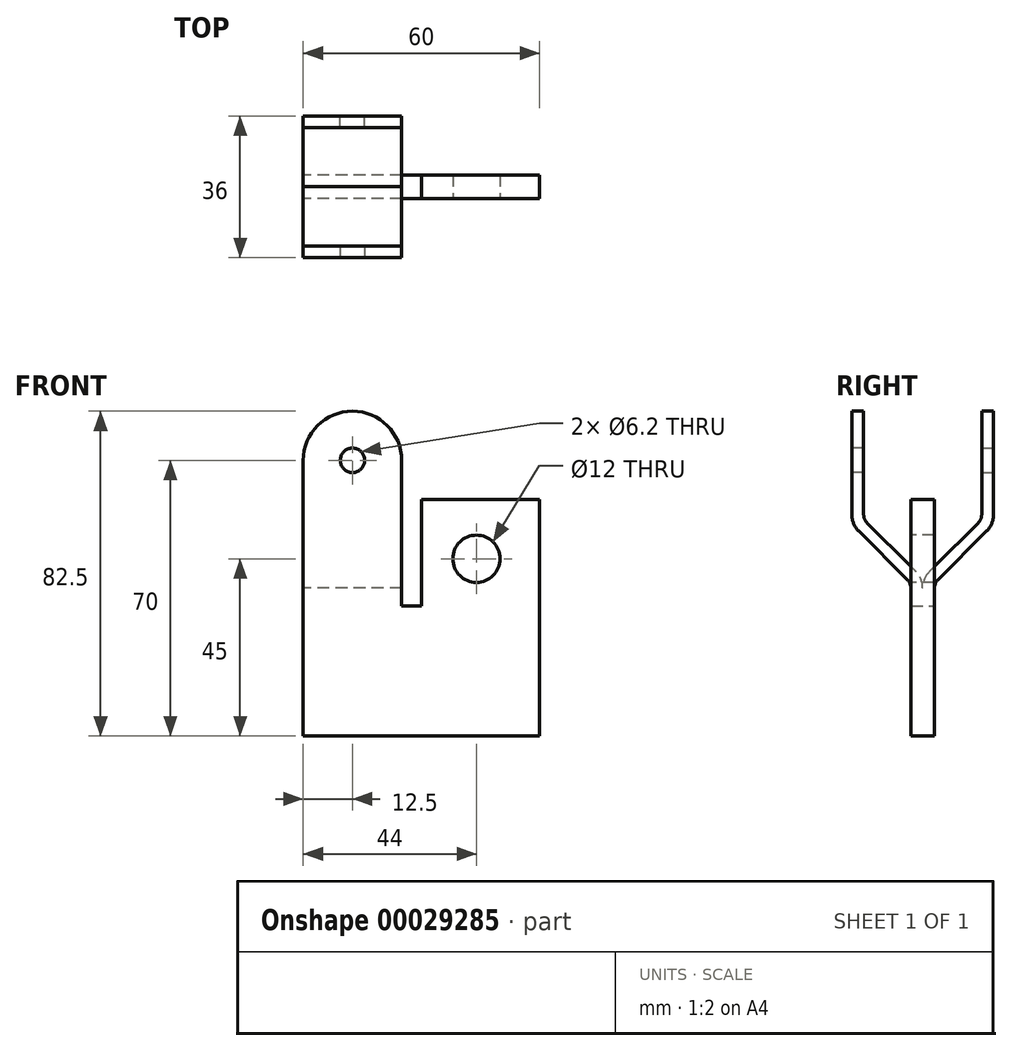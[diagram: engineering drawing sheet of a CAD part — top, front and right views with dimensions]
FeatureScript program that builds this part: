
annotation { "Feature Type Name" : "Feature", "Feature Type Description" : "" }
export const myFeature = defineFeature(function(context is Context, id is Id, definition is map)
    precondition{}
    {
        {
            var Q0;
            Q0=qCreatedBy(makeId("Front.planeOp"),FACE);
            var sketch = newSketch(context, id + "F0", { "sketchPlane" : qUnion([Q0])});
            skLineSegment(sketch, "E0", {"start": v(0, 0) * mm, "end": v(60, 0) * mm});
            skLineSegment(sketch, "E1", {"start": v(60, 0) * mm, "end": v(60, 60) * mm});
            skLineSegment(sketch, "E2", {"start": v(60, 60) * mm, "end": v(30, 60) * mm});
            skLineSegment(sketch, "E3", {"start": v(30, 60) * mm, "end": v(30, 33) * mm});
            skLineSegment(sketch, "E4", {"start": v(30, 33) * mm, "end": v(25, 33) * mm});
            skLineSegment(sketch, "E5", {"start": v(25, 33) * mm, "end": v(25, 35) * mm});
            skLineSegment(sketch, "E6", {"start": v(25, 35) * mm, "end": v(0, 35) * mm});
            skLineSegment(sketch, "E7", {"start": v(0, 35) * mm, "end": v(0, 0) * mm});
            skSolve(sketch);
        }
        {
            var Q0;
            Q0 = qSketchRegion(id + "F0", true);
            extrude(context, id + "F1", {"entities" : qUnion([Q0]), "depth" : 3 * mm});
        }
        {
            var Q0;
            Q0=makeQuery(id+"F1.opExtrude","SWEPT_FACE",FACE,{"disambiguationData":[OSD([sQuery(id+"F0.wireOp",EDGE,"E7")])]});
            var sketch = newSketch(context, id + "F2", { "sketchPlane" : qUnion([Q0])});
            skLineSegment(sketch, "E8", {"start": v(0, 35) * mm, "end": v(0, 40) * mm});
            skLineSegment(sketch, "E9", {"start": v(0, 40) * mm, "end": v(15, 55) * mm});
            skLineSegment(sketch, "E10", {"start": v(15, 55) * mm, "end": v(15, 82.5) * mm});
            skLineSegment(sketch, "E11", {"start": v(15, 82.5) * mm, "end": v(18, 82.5) * mm});
            skLineSegment(sketch, "E12", {"start": v(18, 82.5) * mm, "end": v(18, 53.76) * mm});
            skLineSegment(sketch, "E13", {"start": v(18, 53.76) * mm, "end": v(3, 38.76) * mm});
            skLineSegment(sketch, "E14", {"start": v(3, 38.76) * mm, "end": v(3, 35) * mm});
            skLineSegment(sketch, "E15", {"start": v(3, 35) * mm, "end": v(0, 35) * mm});
            skSolve(sketch);
        }
        {
            var Q0;
            Q0 = qSketchRegion(id + "F2", true);
            var Q1;
            Q1=makeQuery(id+"F1.opExtrude","SWEPT_FACE",FACE,{"disambiguationData":[OSD([sQuery(id+"F0.wireOp",EDGE,"E5")])]});
            extrude(context, id + "F3", {"entities" : qUnion([Q0]), "endBound" : BoundingType.UP_TO_SURFACE, "oppositeDirection" : true, "endBoundEntityFace" : qUnion([Q1]), "depth" : 25 * mm});
        }
        {
            var Q0;
            Q0=makeQuery(id+"F3.opExtrude","SWEPT_BODY",BODY,{"disambiguationData":[OSD([sQuery(id+"F2.wireOp",EDGE,"E8"),sQuery(id+"F2.wireOp",EDGE,"E9"),sQuery(id+"F2.wireOp",EDGE,"E10"),sQuery(id+"F2.wireOp",EDGE,"E11"),sQuery(id+"F2.wireOp",EDGE,"E12"),sQuery(id+"F2.wireOp",EDGE,"E13"),sQuery(id+"F2.wireOp",EDGE,"E14"),sQuery(id+"F2.wireOp",EDGE,"E15")])]});
            var Q1;
            Q1=makeQuery(id+"F1.opExtrude","SWEPT_BODY",BODY,{"disambiguationData":[OSD([sQuery(id+"F0.wireOp",EDGE,"E0"),sQuery(id+"F0.wireOp",EDGE,"E1"),sQuery(id+"F0.wireOp",EDGE,"E2"),sQuery(id+"F0.wireOp",EDGE,"E3"),sQuery(id+"F0.wireOp",EDGE,"E4"),sQuery(id+"F0.wireOp",EDGE,"E5"),sQuery(id+"F0.wireOp",EDGE,"E6"),sQuery(id+"F0.wireOp",EDGE,"E7")])]});
            booleanBodies(context, id + "F4", {"operationType" : BooleanOperationType.UNION, "tools" : qUnion([Q0, Q1])});
        }
        {
            var Q0;
            Q0=makeQuery(id+"F3.opExtrude","SWEPT_EDGE",EDGE,{"disambiguationData":[OSD([sQuery(id+"F2.wireOp",EDGE,"E13"),sQuery(id+"F2.wireOp",EDGE,"E14")])]});
            var Q1;
            Q1=makeQuery(id+"F3.opExtrude","SWEPT_EDGE",EDGE,{"disambiguationData":[OSD([sQuery(id+"F2.wireOp",EDGE,"E9"),sQuery(id+"F2.wireOp",EDGE,"E10")])]});
            fillet(context, id + "F5", {"entities" : qUnion([Q0, Q1]), "radius" : 3 * mm, "tangentPropagation" : true, "allowEdgeOverflow" : false});
        }
        {
            var Q0;
            Q0=makeQuery(id+"F3.opExtrude","SWEPT_EDGE",EDGE,{"disambiguationData":[OSD([sQuery(id+"F2.wireOp",EDGE,"E8"),sQuery(id+"F2.wireOp",EDGE,"E9")])]});
            var Q1;
            Q1=makeQuery(id+"F3.opExtrude","SWEPT_EDGE",EDGE,{"disambiguationData":[OSD([sQuery(id+"F2.wireOp",EDGE,"E12"),sQuery(id+"F2.wireOp",EDGE,"E13")])]});
            fillet(context, id + "F6", {"entities" : qUnion([Q0, Q1]), "radius" : 6 * mm, "tangentPropagation" : true, "allowEdgeOverflow" : false});
        }
        {
            var Q0;
            Q0=makeQuery(id+"F3.opExtrude","SWEPT_FACE",FACE,{"disambiguationData":[OSD([sQuery(id+"F2.wireOp",EDGE,"E12")])]});
            var sketch = newSketch(context, id + "F7", { "sketchPlane" : qUnion([Q0])});
            skCircle(sketch, "E16", {"center": v(12.5, 70) * mm, "radius": 3.1 * mm});
            skSolve(sketch);
        }
        {
            var Q0;
            Q0 = qSketchRegion(id + "F7", true);
            extrude(context, id + "F8", {"entities" : qUnion([Q0]), "operationType" : NewBodyOperationType.REMOVE, "endBound" : BoundingType.UP_TO_NEXT, "oppositeDirection" : true, "depth" : 25 * mm});
        }
        {
            var Q0;
            Q0=makeQuery(id+"F3.opExtrude","CAP_EDGE",EDGE,{"disambiguationData":[OSD([sQuery(id+"F2.wireOp",EDGE,"E11")])],"isStart":true});
            var Q1;
            Q1=makeQuery(id+"F3.opExtrude","CAP_EDGE",EDGE,{"disambiguationData":[OSD([sQuery(id+"F2.wireOp",EDGE,"E11")])],"isStart":false});
            fillet(context, id + "F9", {"entities" : qUnion([Q0, Q1]), "radius" : 12.5 * mm, "tangentPropagation" : true, "allowEdgeOverflow" : false});
        }
        {
            var Q0;
            Q0=makeQuery(id+"F3.opExtrude","SWEPT_BODY",BODY,{"disambiguationData":[OSD([sQuery(id+"F2.wireOp",EDGE,"E8"),sQuery(id+"F2.wireOp",EDGE,"E9"),sQuery(id+"F2.wireOp",EDGE,"E10"),sQuery(id+"F2.wireOp",EDGE,"E11"),sQuery(id+"F2.wireOp",EDGE,"E12"),sQuery(id+"F2.wireOp",EDGE,"E13"),sQuery(id+"F2.wireOp",EDGE,"E14"),sQuery(id+"F2.wireOp",EDGE,"E15")])]});
            var Q1;
            Q1=makeQuery(id+"F4.opBoolean","MERGE",FACE,{"derivedFrom":[makeQuery(id+"F1.opExtrude","CAP_FACE",FACE,{"disambiguationData":[OSD([sQuery(id+"F0.wireOp",EDGE,"E0"),sQuery(id+"F0.wireOp",EDGE,"E1"),sQuery(id+"F0.wireOp",EDGE,"E2"),sQuery(id+"F0.wireOp",EDGE,"E3"),sQuery(id+"F0.wireOp",EDGE,"E4"),sQuery(id+"F0.wireOp",EDGE,"E5"),sQuery(id+"F0.wireOp",EDGE,"E6"),sQuery(id+"F0.wireOp",EDGE,"E7")])],"isStart":true}),makeQuery(id+"F3.opExtrude","SWEPT_FACE",FACE,{"disambiguationData":[OSD([sQuery(id+"F2.wireOp",EDGE,"E8")])]})]});
            mirror(context, id + "F10", {"operationType" : NewBodyOperationType.ADD, "entities" : qUnion([Q0]), "mirrorPlane" : qUnion([Q1])});
        }
        {
            var Q0;
            Q0=makeQuery(id+"F4.opBoolean","MERGE",FACE,{"derivedFrom":[makeQuery(id+"F1.opExtrude","CAP_FACE",FACE,{"disambiguationData":[OSD([sQuery(id+"F0.wireOp",EDGE,"E0"),sQuery(id+"F0.wireOp",EDGE,"E1"),sQuery(id+"F0.wireOp",EDGE,"E2"),sQuery(id+"F0.wireOp",EDGE,"E3"),sQuery(id+"F0.wireOp",EDGE,"E4"),sQuery(id+"F0.wireOp",EDGE,"E5"),sQuery(id+"F0.wireOp",EDGE,"E6"),sQuery(id+"F0.wireOp",EDGE,"E7")])],"isStart":false}),makeQuery(id+"F3.opExtrude","SWEPT_FACE",FACE,{"disambiguationData":[OSD([sQuery(id+"F2.wireOp",EDGE,"E14")])]})]});
            var sketch = newSketch(context, id + "F11", { "sketchPlane" : qUnion([Q0])});
            skCircle(sketch, "E17", {"center": v(44, 45) * mm, "radius": 6 * mm});
            skSolve(sketch);
        }
        {
            var Q0;
            Q0 = qSketchRegion(id + "F11", true);
            extrude(context, id + "F12", {"entities" : qUnion([Q0]), "operationType" : NewBodyOperationType.REMOVE, "endBound" : BoundingType.UP_TO_NEXT, "oppositeDirection" : true, "depth" : 25 * mm});
        }
    });
